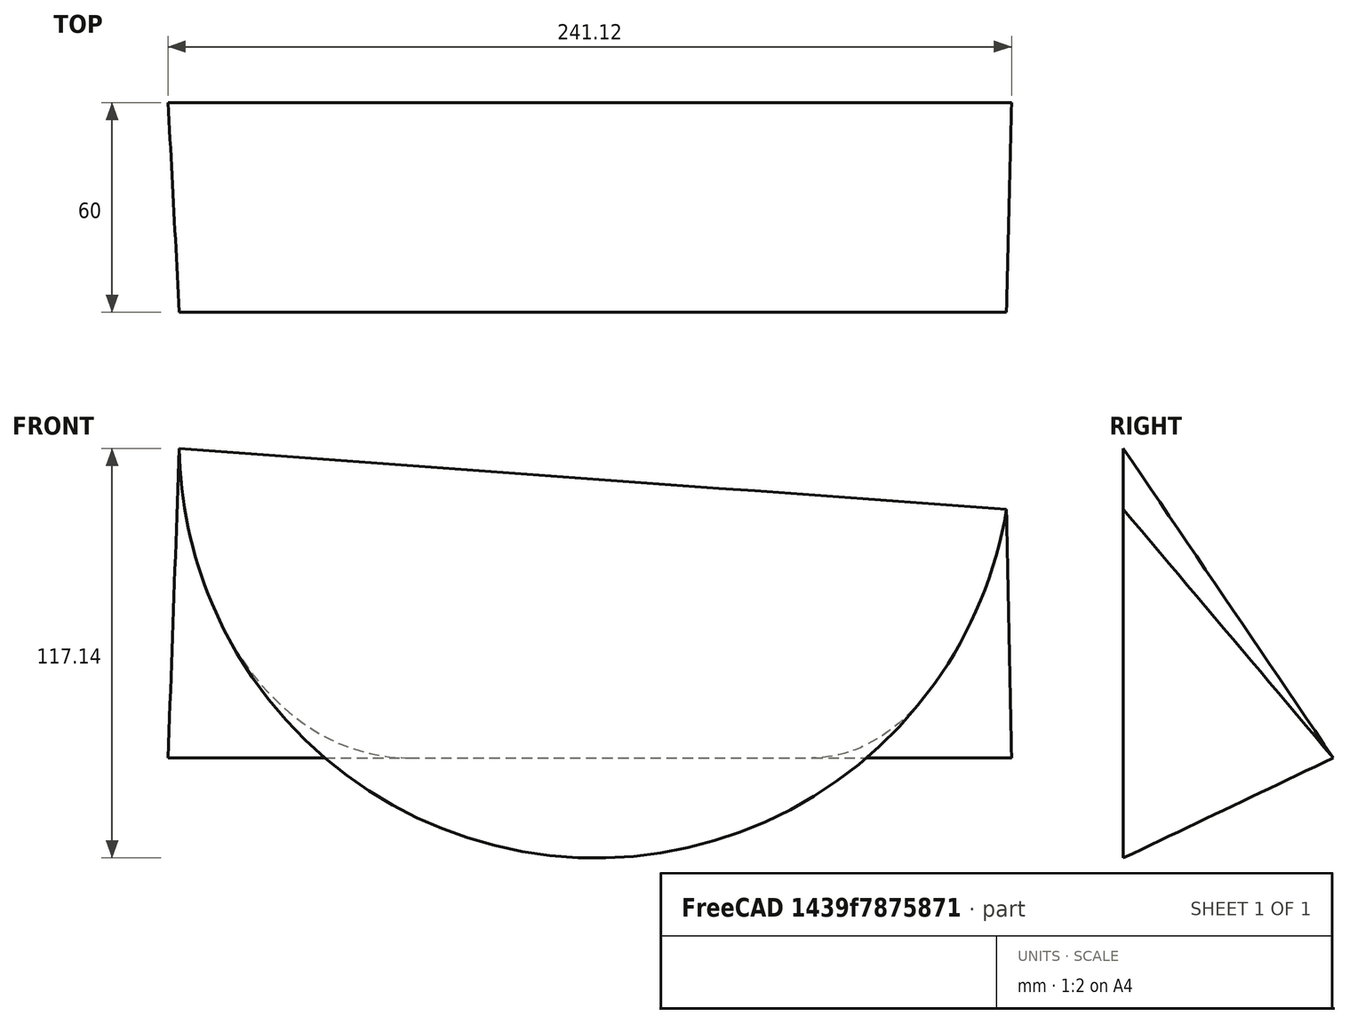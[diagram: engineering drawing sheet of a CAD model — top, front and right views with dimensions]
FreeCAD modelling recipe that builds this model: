
FCSTD DOCUMENT  (FreeCAD 0.21RUnknown)
Label: part10
License: All rights reserved
LicenseURL: http://en.wikipedia.org/wiki/All_rights_reserved
objects: Part::RuledSurface×3, Sketcher::SketchObject×2, Part::Compound×1, Part::Feature×1
note: 7 computed .brp shape members not serialized (recipe doc carries the construction recipe); baked Part::Feature solids carry a one-line shape summary decoded from their .brp

FEATURE [Sketcher::SketchObject] Sketch
  FullyConstrained = false
  Placement = pos=(0,0,0) rot=(1,0,0;1.5708rad)
  sketch-geometry (1):
    g0: ArcOfCircle CenterX=50.2975 CenterY=50.9369 CenterZ=0 NormalX=0 NormalY=0 NormalZ=1 AngleXU=0 Radius=119.032 StartAngle=3.15755 EndAngle=6.12025
FEATURE [Sketcher::SketchObject] Sketch001
  FullyConstrained = false
  Placement = pos=(0,60,0) rot=(1,0,0;1.5708rad)
  sketch-geometry (1):
    g0: LineSegment StartX=-71.9391 StartY=-39.4518 StartZ=0 EndX=169.18 EndY=-39.4518 EndZ=0
  constraints (1):
    c: Horizontal(g0)
FEATURE [Part::RuledSurface] Ruled_Surface
  Curve1 = -> Sketch [Edge1]
  Curve2 = -> Sketch001 [Edge1]
  Orientation = 0
FEATURE [Part::RuledSurface] Ruled_Surface001
  Curve1 = -> Ruled_Surface [Edge4]
  Curve2 = -> Ruled_Surface [Edge2]
  Orientation = 0
FEATURE [Part::RuledSurface] Ruled_Surface003
  Curve1 = -> Sketch [Edge1]
  Curve2 = -> Ruled_Surface001 [Edge2]
  Orientation = 0
FEATURE [Part::Compound] Compound
  Links = -> [Ruled_Surface003,Ruled_Surface,Ruled_Surface001]
FEATURE [Part::Feature] Compound_solid  label="Compound (Solid)"
  shape: bbox 241.1 x 60 x 130.7 mm, 3 faces (baked)
